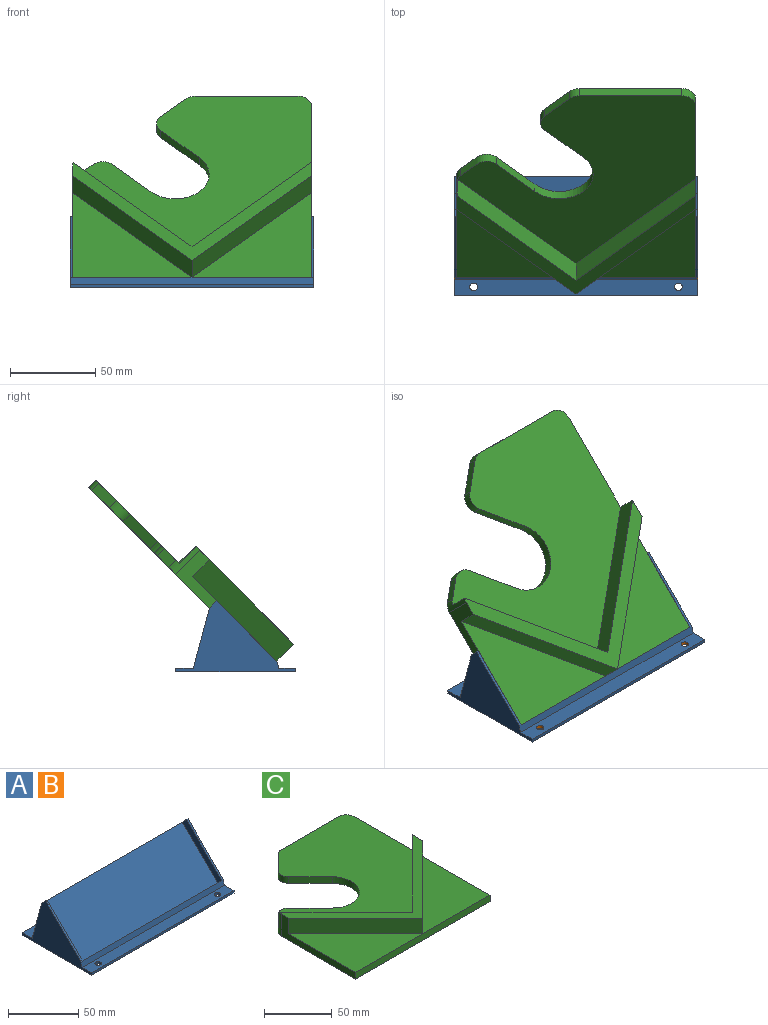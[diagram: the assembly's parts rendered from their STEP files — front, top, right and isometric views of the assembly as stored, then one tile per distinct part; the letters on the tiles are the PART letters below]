
ASSEMBLY  parts=3 mates=1
PART A: 21 faces, bbox 143x70x41.6 mm
  f0: plane 143x9.62mm, normal (0,0,1), area 1343.9mm2, adj f2,f6,f11,f12,f15,f20
  f1: plane 143x2mm, normal (0,1,0), area 286mm2, adj f3,f4,f15,f20
  f2: plane 143x2mm, normal (0,-1,0), area 286mm2, adj f0,f3,f15,f20
  f3: plane 143x70mm, normal (0,0,-1), area 9946.4mm2, adj f1,f2,f9,f10,f11,f12,f15,f20
  f4: plane 143x10.17mm, normal (0,0,1), area 1422.7mm2, adj f1,f8,f9,f10,f15,f20
  f5: plane 140x4.24mm, normal (0,0.71,0.71), area 840mm2, adj f6,f7,f16,f17
  f6: plane 143x4.24mm, normal (0,-0.97,0.26), area 628.1mm2, adj f0,f5,f14,f15,f18,f20
  f7: plane 140x35.36mm, normal (0,-0.71,0.71), area 7000mm2, adj f5,f8,f16,f17
  f8: plane 143x35.36mm, normal (0,0.97,0.26), area 5234.2mm2, adj f4,f7,f13,f15,f19,f20
  f9: cylinder r=2.25mm len=4.5mm, axis (0,0,1), area 28.3mm2, adj f3,f4
  f10: cylinder r=2.25mm len=4.5mm, axis (0,0,1), area 28.3mm2, adj f3,f4
  f11: cylinder r=2.25mm len=4.5mm, axis (0,0,1), area 28.3mm2, adj f0,f3
  f12: cylinder r=2.25mm len=4.5mm, axis (0,0,1), area 28.3mm2, adj f0,f3
  f13: plane 4.24x4.24mm, normal (0,0.71,0.71), area 9mm2, adj f8,f14,f15,f16
  f14: plane 35.36x35.36mm, normal (0,-0.71,0.71), area 75mm2, adj f6,f13,f15,f16
  f15: plane 70x41.6mm, normal (1,0,0), area 1243.9mm2, adj f0,f1,f2,f3,f4,f6,f8,f13
  f16: plane 39.6x39.6mm, normal (-1,0,0), area 300mm2, adj f5,f7,f13,f14
  f17: plane 39.6x39.6mm, normal (1,0,0), area 300mm2, adj f5,f7,f18,f19
  f18: plane 35.36x35.36mm, normal (0,-0.71,0.71), area 75mm2, adj f6,f17,f19,f20
  f19: plane 4.24x4.24mm, normal (0,0.71,0.71), area 9mm2, adj f8,f17,f18,f20
  f20: plane 70x41.6mm, normal (-1,0,0), area 1243.9mm2, adj f0,f1,f2,f3,f4,f6,f8,f18
PART B: same geometry as A
PART C: 22 faces, bbox 140x150x20 mm
  f0: plane 150x140mm, normal (0,0,-1), area 16372mm2, adj f3,f4,f5,f6,f12,f13,f14,f15
  f1: plane 140x70.05mm, normal (0,0,1), area 4906.5mm2, adj f4,f5,f6,f9,f10
  f2: plane 139.49x138.64mm, normal (0,0,1), area 9882.2mm2, adj f3,f6,f7,f8,f12,f13,f14,f15
  f3: plane 60.05x6mm, normal (0,1,0), area 360.3mm2, adj f0,f2,f18,f21
  f4: plane 78.05x20mm, normal (-1,0,0), area 580.3mm2, adj f0,f1,f5,f9,f11,f19
  f5: plane 140x6mm, normal (0,-1,0), area 840mm2, adj f0,f1,f4,f6
  f6: plane 142x20mm, normal (1,0,0), area 1010.4mm2, adj f0,f1,f2,f5,f7,f10,f11,f21
  f7: plane 70x70mm, normal (-0.71,0.71,0), area 1385.9mm2, adj f2,f6,f8,f11
  f8: plane 69.49x69.49mm, normal (0.71,0.71,0), area 1375.9mm2, adj f2,f7,f11,f19
  f9: plane 70x70mm, normal (-0.71,-0.71,0), area 1385.9mm2, adj f1,f4,f10,f11
  f10: plane 70x70mm, normal (0.71,-0.71,0), area 1385.9mm2, adj f1,f6,f9,f11
  f11: plane 140x81.31mm, normal (0,0,1), area 1583.3mm2, adj f4,f6,f7,f8,f9,f10,f19
  f12: plane 9.68x9.68mm, normal (-0.71,0.71,0), area 82.1mm2, adj f0,f2,f19,f20
  f13: plane 22.63x22.63mm, normal (0.71,0.71,0), area 192mm2, adj f0,f2,f15,f20
  f14: plane 22.63x22.63mm, normal (-0.71,-0.71,0), area 192mm2, adj f0,f2,f15,f17
  f15: cylinder r=20mm len=34.14mm, axis (0,0,1), area 377mm2, adj f0,f2,f13,f14
  f16: plane 14.68x14.68mm, normal (-0.71,0.71,0), area 124.5mm2, adj f0,f2,f17,f18
  f17: cylinder r=8mm len=11.31mm, axis (0,0,1), area 75.4mm2, adj f0,f2,f14,f16
  f18: cylinder r=8mm len=6mm, axis (0,0,1), area 37.7mm2, adj f0,f2,f3,f16
  f19: cylinder r=8mm len=20mm, axis (0,0,-1), area 77.8mm2, adj f0,f2,f4,f8,f11,f12
  f20: cylinder r=8mm len=11.31mm, axis (0,0,-1), area 75.4mm2, adj f0,f2,f12,f13
  f21: cylinder r=8mm len=8mm, axis (0,0,1), area 75.4mm2, adj f0,f2,f3,f6
PLACE A t=(-15.65,-13.74,-6.25)mm
PLACE B t=(-15.65,-13.74,-6.25)mm
PLACE C rot(axis=(1,0,0),45deg) t=(-15.65,35.05,51.03)mm
MATE fastened C.f5 <-> A.f5  axis (0,-0.71,-0.71) through (-15.65,-15.86,-4.12)mm
